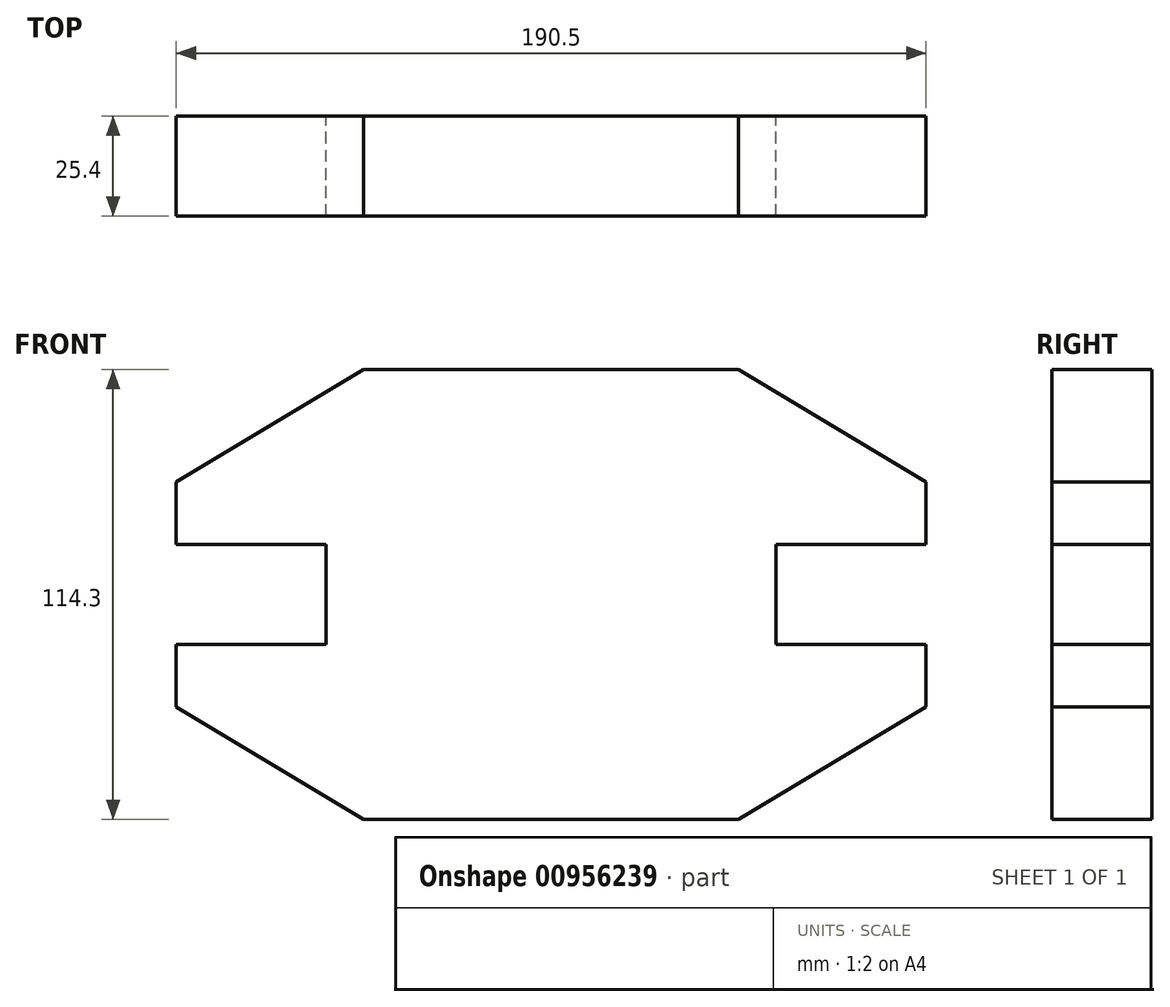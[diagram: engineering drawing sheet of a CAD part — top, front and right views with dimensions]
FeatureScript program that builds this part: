
annotation { "Feature Type Name" : "Feature", "Feature Type Description" : "" }
export const myFeature = defineFeature(function(context is Context, id is Id, definition is map)
    precondition{}
    {
        {
            var Q0;
            Q0=qCreatedBy(makeId("Front.planeOp"),FACE);
            var sketch = newSketch(context, id + "F0", { "sketchPlane" : qUnion([Q0])});
            skLineSegment(sketch, "E0", {"start": v(0, 57.15) * mm, "end": v(47.63, 57.15) * mm});
            skLineSegment(sketch, "E1", {"start": v(0, 57.15) * mm, "end": v(-47.62, 57.15) * mm});
            skLineSegment(sketch, "E2", {"start": v(-95.25, 28.57) * mm, "end": v(-95.25, 12.7) * mm});
            skLineSegment(sketch, "E3", {"start": v(95.25, 28.57) * mm, "end": v(95.25, 12.7) * mm});
            skLineSegment(sketch, "E4", {"start": v(-95.25, 28.57) * mm, "end": v(-47.62, 57.15) * mm});
            skLineSegment(sketch, "E5", {"start": v(47.62, 57.15) * mm, "end": v(95.25, 28.57) * mm});
            skLineSegment(sketch, "E6", {"start": v(-95.25, 12.7) * mm, "end": v(-57.15, 12.7) * mm});
            skLineSegment(sketch, "E7", {"start": v(57.15, 12.7) * mm, "end": v(95.25, 12.7) * mm});
            skLineSegment(sketch, "E8", {"start": v(-57.15, 12.7) * mm, "end": v(-57.15, -12.7) * mm});
            skLineSegment(sketch, "E9", {"start": v(57.15, 12.7) * mm, "end": v(57.15, -12.7) * mm});
            skLineSegment(sketch, "E10", {"start": v(-57.15, -12.7) * mm, "end": v(-95.25, -12.7) * mm});
            skLineSegment(sketch, "E11", {"start": v(57.15, -12.7) * mm, "end": v(95.25, -12.7) * mm});
            skLineSegment(sketch, "E12", {"start": v(-95.25, -12.7) * mm, "end": v(-95.25, -28.58) * mm});
            skLineSegment(sketch, "E13", {"start": v(95.25, -12.7) * mm, "end": v(95.25, -28.57) * mm});
            skLineSegment(sketch, "E14", {"start": v(-95.25, -28.58) * mm, "end": v(-47.62, -57.15) * mm});
            skLineSegment(sketch, "E15", {"start": v(47.63, -57.15) * mm, "end": v(95.25, -28.57) * mm});
            skLineSegment(sketch, "E16", {"start": v(-47.62, -57.15) * mm, "end": v(47.62, -57.15) * mm});
            skPoint(sketch, "E17.middle", {"position": v(0, 0) * mm});
            skLineSegment(sketch, "E18", {"start": v(-38.18, 0) * mm, "end": v(0, 38.17) * mm});
            skLineSegment(sketch, "E19", {"start": v(0, 38.17) * mm, "end": v(38.18, 0) * mm});
            skLineSegment(sketch, "E20", {"start": v(38.18, 0) * mm, "end": v(0, -38.18) * mm});
            skLineSegment(sketch, "E21", {"start": v(0.3, -37.2) * mm, "end": v(-38.18, 0) * mm});
            skSolve(sketch);
        }
        {
            var Q0;
            Q0=makeQuery(id+"F0.imprint","IMPRINT",FACE,{"disambiguationData":[TD([[makeQuery(id+"F0.imprint","IMPRINT",EDGE,{"derivedFrom":sQuery(id+"F0.wireOp",EDGE,"E0")}),-1.0]])]});
            var sketch = newSketch(context, id + "F1", { "sketchPlane" : qUnion([Q0])});
            skSolve(sketch);
        }
        {
            var Q0;
            Q0 = qSketchRegion(id + "F0", true);
            extrude(context, id + "F2", {"entities" : qUnion([Q0]), "depth" : 25.4 * mm, "offsetDistance" : 25.4 * mm});
        }
        {
            var Q0;
            Q0 = qSketchRegion(id + "F0", true);
            extrude(context, id + "F3", {"entities" : qUnion([Q0]), "operationType" : NewBodyOperationType.REMOVE, "oppositeDirection" : true, "depth" : 25.4 * mm, "offsetDistance" : 25.4 * mm});
        }
    });
